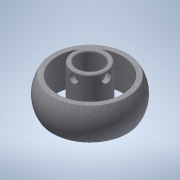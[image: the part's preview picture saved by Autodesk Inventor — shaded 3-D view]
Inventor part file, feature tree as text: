
AUTODESK INVENTOR PART (.ipt)
format: ipt  version: 2021 (Build 250183000, 183)  size: 211,968 bytes
history: native  units: mm
features: extrude x4, fillet x1, revolve x1, plane x1, sketch x1
ambient origin geometry x8: Origin, YZ Plane, XZ Plane, XY Plane, X Axis, Y Axis, Z Axis, Center Point
bodies: Solid1 (feature_tree)
feature tree (8):
  extrude  "Extrusion1"  Depth=3.0mm
  extrude  "Extrusion2"  Depth=20.0mm
  extrude  "Extrusion3"  Depth=3.0mm
  extrude  "Extrusion4"  Depth=20.5mm TaperAngle=0.0deg
  fillet  "Fillet1"  Radius=4.0mm
  revolve  "Revolution1"  [1 undecoded]
  plane  "Work Plane1"
  sketch  "Sketch5"  dims[d0=48.0mm d1=3.0mm d2=16.0mm d3=3.0mm d4=20.5mm d5=0.0mm d6=28.5mm d7=4.0mm d8=0.0mm d9=0.0mm d10=4.0mm d11=6.0mm d12=28.5mm d13=0.0mm d14=4.0mm d15=6.0mm d16=28.5mm d17=0.0mm d18=1.0mm d19=20.0mm d20=90.0deg]
note: 1 required parameter value undecoded (feature->parameter linkage not recoverable at this tier; creation-order binding heuristic only, values carry confidence <= 0.55)
